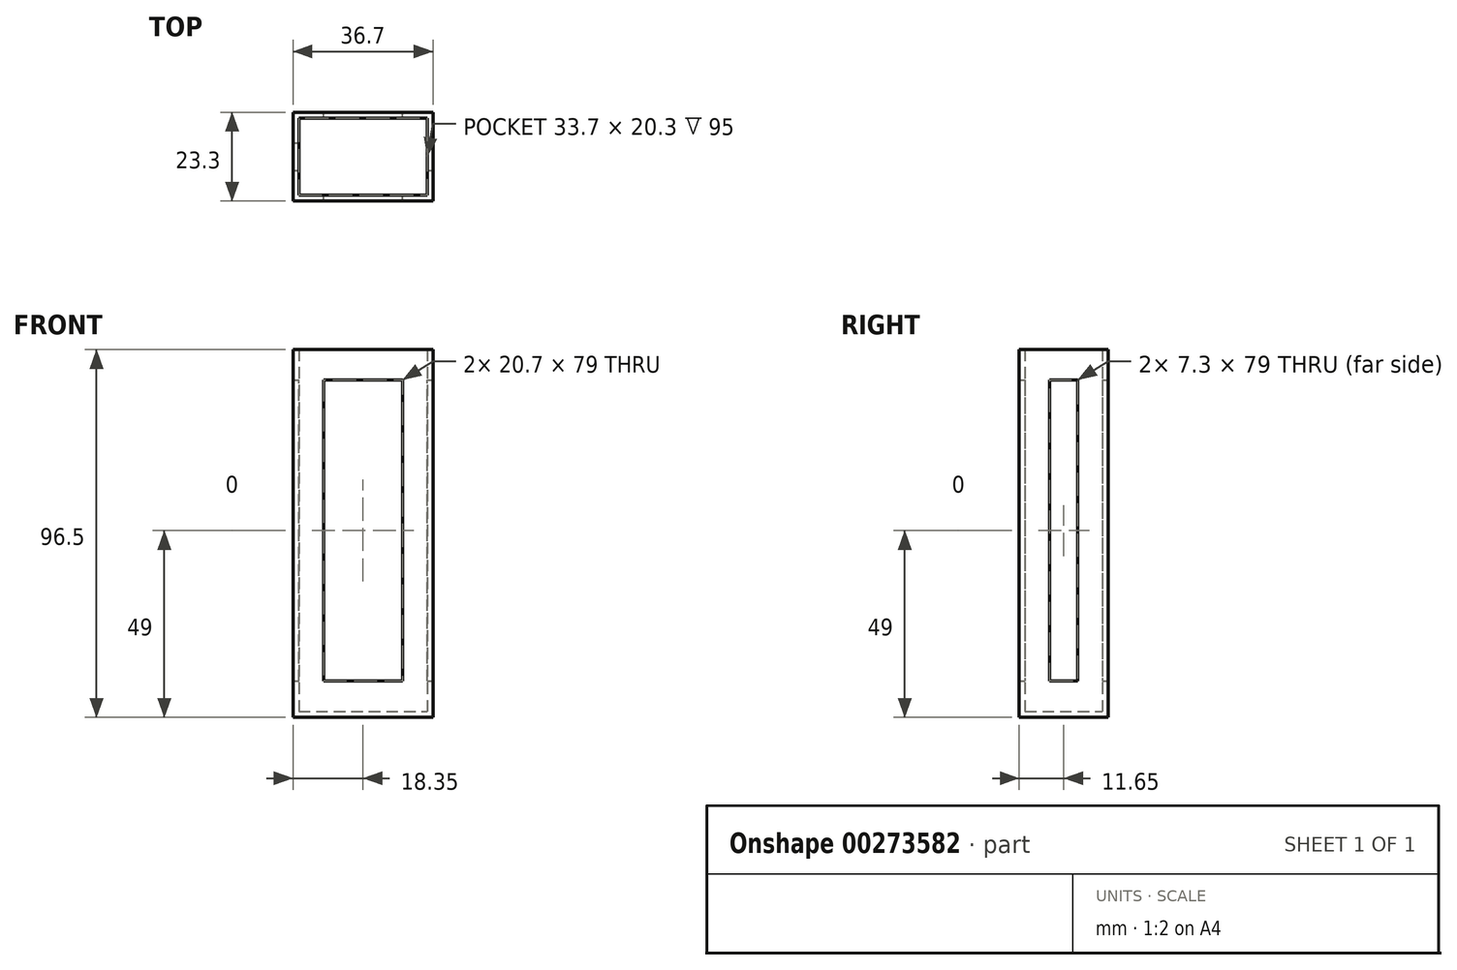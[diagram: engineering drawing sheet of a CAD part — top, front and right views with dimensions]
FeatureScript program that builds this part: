
annotation { "Feature Type Name" : "Feature", "Feature Type Description" : "" }
export const myFeature = defineFeature(function(context is Context, id is Id, definition is map)
    precondition{}
    {
        {
            var Q0;
            Q0=qCreatedBy(makeId("Top.planeOp"),FACE);
            var sketch = newSketch(context, id + "F0", { "sketchPlane" : qUnion([Q0])});
            skLineSegment(sketch, "E0.bottom", {"start": v(0, 0) * mm, "end": v(33.7, 0) * mm});
            skLineSegment(sketch, "E0.top", {"start": v(0, 20.3) * mm, "end": v(33.7, 20.3) * mm});
            skLineSegment(sketch, "E0.left", {"start": v(0, 0) * mm, "end": v(0, 20.3) * mm});
            skLineSegment(sketch, "E0.right", {"start": v(33.7, 0) * mm, "end": v(33.7, 20.3) * mm});
            skLineSegment(sketch, "E1.0", {"start": v(-1.5, -1.5) * mm, "end": v(35.2, -1.5) * mm});
            skLineSegment(sketch, "E1.1", {"start": v(-1.5, -1.5) * mm, "end": v(-1.5, 21.8) * mm});
            skLineSegment(sketch, "E1.2", {"start": v(-1.5, 21.8) * mm, "end": v(35.2, 21.8) * mm});
            skLineSegment(sketch, "E1.3", {"start": v(35.2, -1.5) * mm, "end": v(35.2, 21.8) * mm});
            skSolve(sketch);
        }
        {
            var Q0;
            Q0=qSketchRegion(id+"F0",true);
            extrude(context, id + "F1", {"entities" : qUnion([Q0]), "depth" : 95 * mm});
        }
        {
            var Q0;
            Q0=makeQuery(id+"F1.opExtrude","SWEPT_FACE",FACE,{"disambiguationData":[OSD([sQuery(id+"F0.wireOp",EDGE,"E1.2")])]});
            var sketch = newSketch(context, id + "F2", { "sketchPlane" : qUnion([Q0])});
            skLineSegment(sketch, "E2.0", {"start": v(-6.5, 87) * mm, "end": v(-6.5, 8) * mm});
            skLineSegment(sketch, "E2.1", {"start": v(-6.5, 87) * mm, "end": v(-27.2, 87) * mm});
            skLineSegment(sketch, "E2.2", {"start": v(-27.2, 87) * mm, "end": v(-27.2, 8) * mm});
            skLineSegment(sketch, "E2.3", {"start": v(-6.5, 8) * mm, "end": v(-27.2, 8) * mm});
            skSolve(sketch);
        }
        {
            var Q0;
            Q0=qSketchRegion(id+"F2",true);
            extrude(context, id + "F3", {"entities" : qUnion([Q0]), "operationType" : NewBodyOperationType.REMOVE, "endBound" : BoundingType.THROUGH_ALL, "oppositeDirection" : true, "depth" : 25 * mm});
        }
        {
            var Q0;
            Q0=makeQuery(id+"F1.opExtrude","SWEPT_FACE",FACE,{"disambiguationData":[OSD([sQuery(id+"F0.wireOp",EDGE,"E1.3")])]});
            var sketch = newSketch(context, id + "F4", { "sketchPlane" : qUnion([Q0])});
            skLineSegment(sketch, "E3.0", {"start": v(6.5, 8) * mm, "end": v(13.8, 8) * mm});
            skLineSegment(sketch, "E3.1", {"start": v(6.5, 87) * mm, "end": v(6.5, 8) * mm});
            skLineSegment(sketch, "E3.2", {"start": v(13.8, 87) * mm, "end": v(6.5, 87) * mm});
            skLineSegment(sketch, "E3.3", {"start": v(13.8, 8) * mm, "end": v(13.8, 87) * mm});
            skSolve(sketch);
        }
        {
            var Q0;
            Q0=qSketchRegion(id+"F4",true);
            extrude(context, id + "F5", {"entities" : qUnion([Q0]), "operationType" : NewBodyOperationType.REMOVE, "endBound" : BoundingType.THROUGH_ALL, "oppositeDirection" : true, "depth" : 25 * mm});
        }
        {
            var Q0;
            Q0=qCreatedBy(makeId("Top.planeOp"),FACE);
            var sketch = newSketch(context, id + "F6", { "sketchPlane" : qUnion([Q0])});
            skLineSegment(sketch, "E4.0", {"start": v(-1.5, -1.5) * mm, "end": v(35.2, -1.5) * mm});
            skLineSegment(sketch, "E5.0", {"start": v(-1.5, -1.5) * mm, "end": v(-1.5, 21.8) * mm});
            skLineSegment(sketch, "E6.0", {"start": v(-1.5, 21.8) * mm, "end": v(35.2, 21.8) * mm});
            skLineSegment(sketch, "E7.0", {"start": v(35.2, -1.5) * mm, "end": v(35.2, 21.8) * mm});
            skSolve(sketch);
        }
        {
            var Q0;
            Q0=qSketchRegion(id+"F6",true);
            extrude(context, id + "F7", {"entities" : qUnion([Q0]), "operationType" : NewBodyOperationType.ADD, "oppositeDirection" : true, "depth" : 1.5 * mm});
        }
    });
